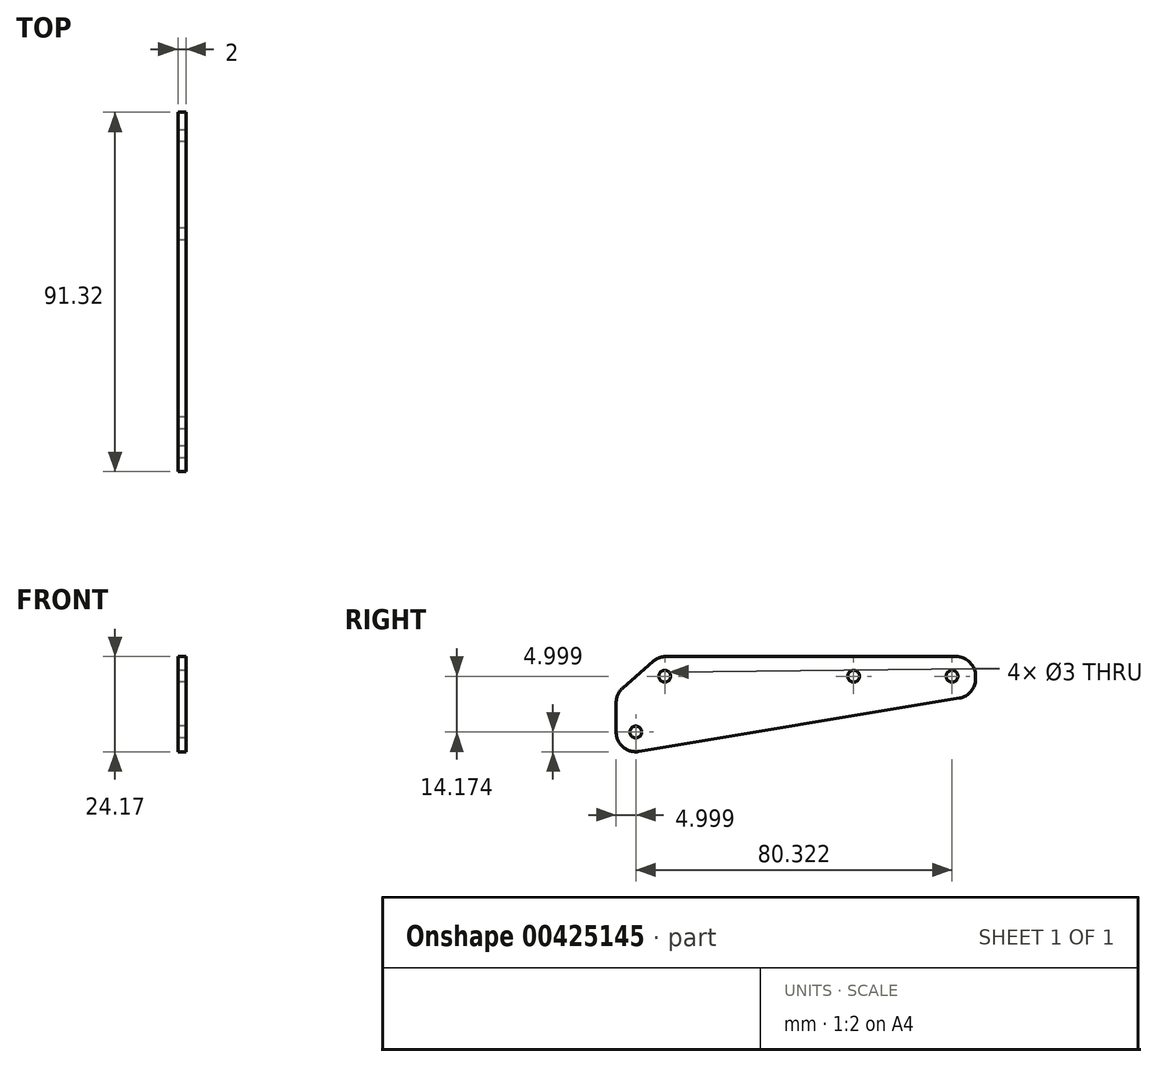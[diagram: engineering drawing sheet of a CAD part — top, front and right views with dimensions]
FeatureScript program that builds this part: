
annotation { "Feature Type Name" : "Feature", "Feature Type Description" : "" }
export const myFeature = defineFeature(function(context is Context, id is Id, definition is map)
    precondition{}
    {
        {
            var Q0;
            Q0=qCreatedBy(makeId("Right.planeOp"),FACE);
            var sketch = newSketch(context, id + "F0", { "sketchPlane" : qUnion([Q0])});
            skLineSegment(sketch, "E0", {"start": v(-31.25, 32.46) * mm, "end": v(42.45, 32.46) * mm});
            skLineSegment(sketch, "E1", {"start": v(47.45, 27.46) * mm, "end": v(47.45, 26.84) * mm});
            skLineSegment(sketch, "E2", {"start": v(43.27, 21.91) * mm, "end": v(-38.05, 8.36) * mm});
            skLineSegment(sketch, "E3", {"start": v(-43.87, 13.29) * mm, "end": v(-43.87, 20.79) * mm});
            skLineSegment(sketch, "E4", {"start": v(-42.16, 24.55) * mm, "end": v(-34.54, 31.22) * mm});
            skPoint(sketch, "E5.visualSharp", {"position": v(47.45, 32.46) * mm});
            skArc(sketch, "E5.filletArc", {"start": v(47.45, 27.46) * mm, "mid": v(45.99, 31) * mm, "end": v(42.45, 32.46) * mm});
            skPoint(sketch, "E6.visualSharp", {"position": v(47.45, 22.6) * mm});
            skArc(sketch, "E6.filletArc", {"start": v(43.27, 21.91) * mm, "mid": v(46.27, 23.61) * mm, "end": v(47.45, 26.84) * mm});
            skPoint(sketch, "E7.visualSharp", {"position": v(-43.87, 7.39) * mm});
            skArc(sketch, "E7.filletArc", {"start": v(-43.87, 13.29) * mm, "mid": v(-42.1, 9.47) * mm, "end": v(-38.05, 8.36) * mm});
            skPoint(sketch, "E8.visualSharp", {"position": v(-33.13, 32.46) * mm});
            skArc(sketch, "E8.filletArc", {"start": v(-31.25, 32.46) * mm, "mid": v(-33, 32.14) * mm, "end": v(-34.54, 31.22) * mm});
            skPoint(sketch, "E9.visualSharp", {"position": v(-43.87, 23.05) * mm});
            skArc(sketch, "E9.filletArc", {"start": v(-42.16, 24.55) * mm, "mid": v(-43.42, 22.85) * mm, "end": v(-43.87, 20.79) * mm});
            skSolve(sketch);
        }
        {
            var Q0;
            Q0=qSketchRegion(id+"F0",true);
            extrude(context, id + "F1", {"entities" : qUnion([Q0]), "depth" : 2 * mm});
        }
        {
            var Q0;
            Q0=qCreatedBy(makeId("Right.planeOp"),FACE);
            var sketch = newSketch(context, id + "F2", { "sketchPlane" : qUnion([Q0])});
            skPoint(sketch, "E10", {"position": v(41.45, 27.46) * mm});
            skPoint(sketch, "E11", {"position": v(16.45, 27.46) * mm});
            skSolve(sketch);
        }
        {
            var Q0;
            Q0=sQuery(id+"F2.wireOp",VERTEX,"E10");
            var Q1;
            Q1=sQuery(id+"F2.wireOp",VERTEX,"E11");
            var Q2;
            Q2=makeQuery(id+"F1.opExtrude","SWEPT_BODY",BODY,{"disambiguationData":[OSD([sQuery(id+"F0.wireOp",EDGE,"E0"),sQuery(id+"F0.wireOp",EDGE,"E1"),sQuery(id+"F0.wireOp",EDGE,"E2"),sQuery(id+"F0.wireOp",EDGE,"E3"),sQuery(id+"F0.wireOp",EDGE,"E4"),sQuery(id+"F0.wireOp",EDGE,"E5.filletArc"),sQuery(id+"F0.wireOp",EDGE,"E6.filletArc"),sQuery(id+"F0.wireOp",EDGE,"E7.filletArc"),sQuery(id+"F0.wireOp",EDGE,"E8.filletArc"),sQuery(id+"F0.wireOp",EDGE,"E9.filletArc")])]});
            hole(context, id + "F3", {"style" : HoleStyle.SIMPLE, "endStyle" : HoleEndStyle.THROUGH, "oppositeDirection" : true, "holeDiameter" : 3 * mm, "isTappedThrough" : true, "tappedDepth" : 12 * mm, "tapClearance" : 3, "locations" : qUnion([Q0, Q1]), "scope" : qUnion([Q2])});
        }
        {
            var Q0;
            Q0=qCreatedBy(makeId("Right.planeOp"),FACE);
            var sketch = newSketch(context, id + "F4", { "sketchPlane" : qUnion([Q0])});
            skPoint(sketch, "E12", {"position": v(-38.87, 13.29) * mm});
            skPoint(sketch, "E13", {"position": v(-31.52, 27.46) * mm});
            skSolve(sketch);
        }
        {
            var Q0;
            Q0=sQuery(id+"F4.wireOp",VERTEX,"E13");
            var Q1;
            Q1=sQuery(id+"F4.wireOp",VERTEX,"E12");
            var Q2;
            Q2=makeQuery(id+"F1.opExtrude","SWEPT_BODY",BODY,{"disambiguationData":[OSD([sQuery(id+"F0.wireOp",EDGE,"E0"),sQuery(id+"F0.wireOp",EDGE,"E1"),sQuery(id+"F0.wireOp",EDGE,"E2"),sQuery(id+"F0.wireOp",EDGE,"E3"),sQuery(id+"F0.wireOp",EDGE,"E4"),sQuery(id+"F0.wireOp",EDGE,"E5.filletArc"),sQuery(id+"F0.wireOp",EDGE,"E6.filletArc"),sQuery(id+"F0.wireOp",EDGE,"E7.filletArc"),sQuery(id+"F0.wireOp",EDGE,"E8.filletArc"),sQuery(id+"F0.wireOp",EDGE,"E9.filletArc")])]});
            hole(context, id + "F5", {"style" : HoleStyle.SIMPLE, "endStyle" : HoleEndStyle.THROUGH, "oppositeDirection" : true, "holeDiameter" : 3 * mm, "isTappedThrough" : true, "tappedDepth" : 12 * mm, "tapClearance" : 3, "locations" : qUnion([Q0, Q1]), "scope" : qUnion([Q2])});
        }
    });
